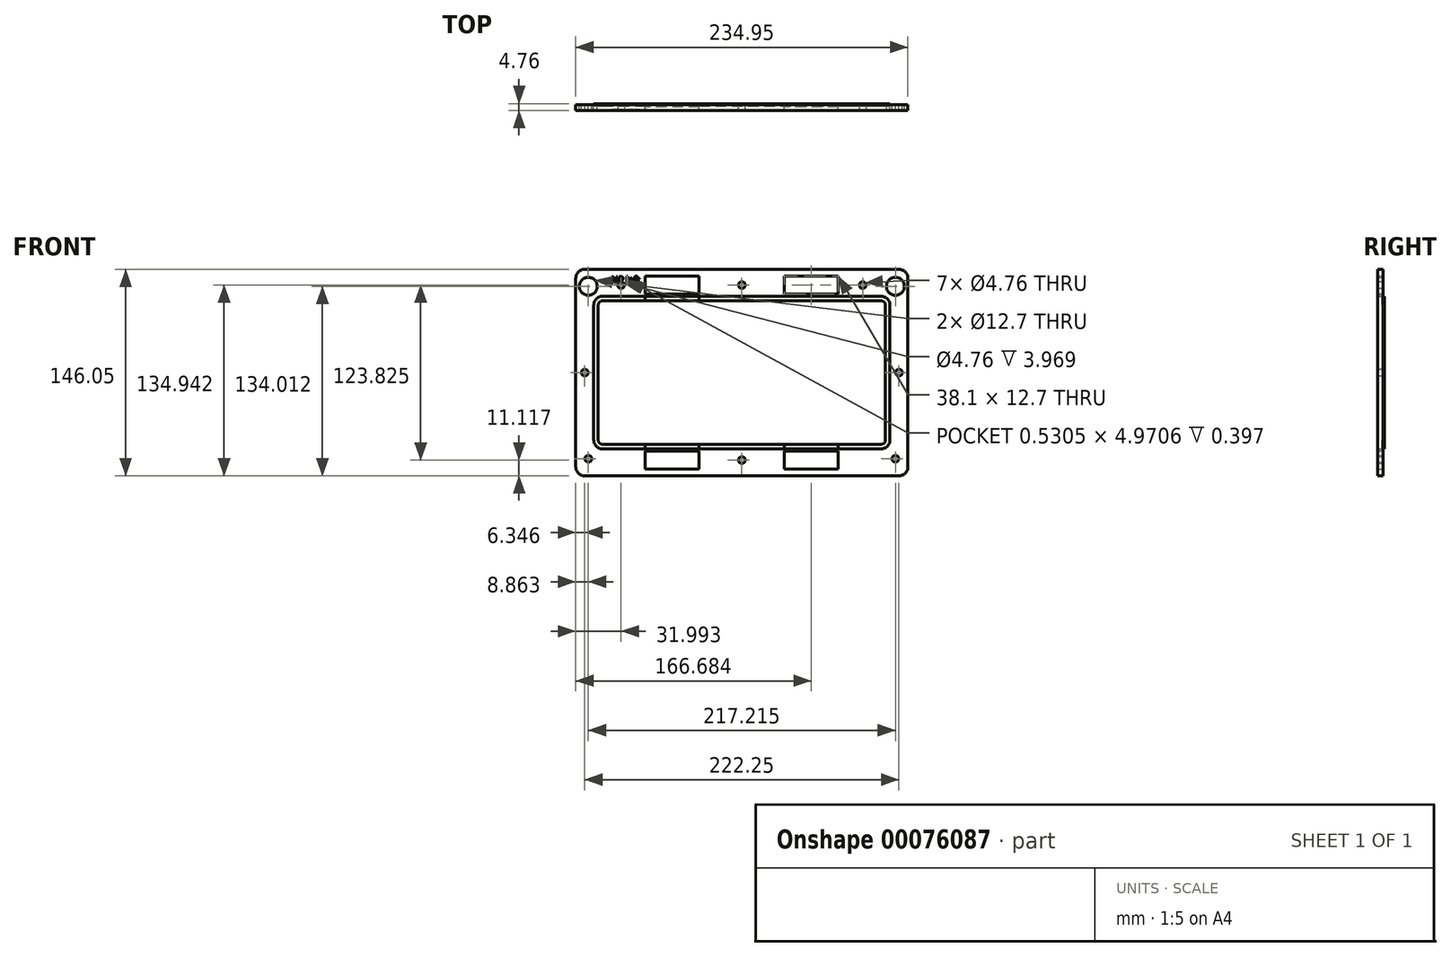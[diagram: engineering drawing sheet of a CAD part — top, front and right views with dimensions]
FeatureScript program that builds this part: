
annotation { "Feature Type Name" : "Feature", "Feature Type Description" : "" }
export const myFeature = defineFeature(function(context is Context, id is Id, definition is map)
    precondition{}
    {
        {
            var Q0;
            Q0=qCreatedBy(makeId("Front.planeOp"),FACE);
            var sketch = newSketch(context, id + "F0", { "sketchPlane" : qUnion([Q0])});
            skLineSegment(sketch, "E0.bottom", {"start": v(-85.43, 54.25) * mm, "end": v(111.42, 54.25) * mm});
            skLineSegment(sketch, "E0.top", {"start": v(-85.43, -53.7) * mm, "end": v(111.42, -53.7) * mm});
            skLineSegment(sketch, "E0.left", {"start": v(-91.78, 47.9) * mm, "end": v(-91.78, -47.35) * mm});
            skLineSegment(sketch, "E0.right", {"start": v(117.77, 47.9) * mm, "end": v(117.77, -47.35) * mm});
            skPoint(sketch, "E1.visualSharp", {"position": v(-91.78, 54.25) * mm});
            skArc(sketch, "E1.filletArc", {"start": v(-85.43, 54.25) * mm, "mid": v(-89.92, 52.4) * mm, "end": v(-91.78, 47.9) * mm});
            skPoint(sketch, "E2.visualSharp", {"position": v(117.77, 54.25) * mm});
            skArc(sketch, "E2.filletArc", {"start": v(117.77, 47.9) * mm, "mid": v(115.9, 52.4) * mm, "end": v(111.42, 54.25) * mm});
            skPoint(sketch, "E3.visualSharp", {"position": v(117.77, -53.7) * mm});
            skArc(sketch, "E3.filletArc", {"start": v(111.42, -53.7) * mm, "mid": v(115.9, -51.84) * mm, "end": v(117.77, -47.35) * mm});
            skPoint(sketch, "E4.visualSharp", {"position": v(-91.78, -53.7) * mm});
            skArc(sketch, "E4.filletArc", {"start": v(-91.78, -47.35) * mm, "mid": v(-89.92, -51.84) * mm, "end": v(-85.43, -53.7) * mm});
            skArc(sketch, "E5.0", {"start": v(-85.43, 51.08) * mm, "mid": v(-87.68, 50.15) * mm, "end": v(-88.6, 47.9) * mm});
            skLineSegment(sketch, "E5.1", {"start": v(-88.6, 47.9) * mm, "end": v(-88.6, -47.35) * mm});
            skLineSegment(sketch, "E5.2", {"start": v(-85.43, 51.08) * mm, "end": v(111.42, 51.08) * mm});
            skArc(sketch, "E5.3", {"start": v(-88.6, -47.35) * mm, "mid": v(-87.68, -49.6) * mm, "end": v(-85.43, -50.52) * mm});
            skArc(sketch, "E5.4", {"start": v(114.6, 47.9) * mm, "mid": v(113.66, 50.15) * mm, "end": v(111.42, 51.08) * mm});
            skLineSegment(sketch, "E5.5", {"start": v(114.6, 47.9) * mm, "end": v(114.6, -47.35) * mm});
            skArc(sketch, "E5.6", {"start": v(111.42, -50.52) * mm, "mid": v(113.66, -49.6) * mm, "end": v(114.6, -47.35) * mm});
            skLineSegment(sketch, "E5.7", {"start": v(-85.43, -50.52) * mm, "end": v(111.42, -50.52) * mm});
            skLineSegment(sketch, "E6.0", {"start": v(-98.13, 73.3) * mm, "end": v(124.12, 73.3) * mm});
            skLineSegment(sketch, "E7.0", {"start": v(-98.13, -72.75) * mm, "end": v(124.12, -72.75) * mm});
            skLineSegment(sketch, "E8.0", {"start": v(-104.48, 66.95) * mm, "end": v(-104.48, -66.4) * mm});
            skLineSegment(sketch, "E9.0", {"start": v(130.47, 66.95) * mm, "end": v(130.47, -66.4) * mm});
            skPoint(sketch, "E10.visualSharp", {"position": v(-104.48, 73.3) * mm});
            skArc(sketch, "E10.filletArc", {"start": v(-98.13, 73.3) * mm, "mid": v(-102.62, 71.44) * mm, "end": v(-104.48, 66.95) * mm});
            skPoint(sketch, "E11.visualSharp", {"position": v(130.47, 73.3) * mm});
            skArc(sketch, "E11.filletArc", {"start": v(130.47, 66.95) * mm, "mid": v(128.6, 71.44) * mm, "end": v(124.12, 73.3) * mm});
            skPoint(sketch, "E12.visualSharp", {"position": v(130.47, -72.75) * mm});
            skArc(sketch, "E12.filletArc", {"start": v(124.12, -72.75) * mm, "mid": v(128.6, -70.89) * mm, "end": v(130.47, -66.4) * mm});
            skPoint(sketch, "E13.visualSharp", {"position": v(-104.48, -72.75) * mm});
            skArc(sketch, "E13.filletArc", {"start": v(-104.48, -66.4) * mm, "mid": v(-102.62, -70.89) * mm, "end": v(-98.13, -72.75) * mm});
            skLineSegment(sketch, "E14", {"start": v(-104.48, 66.95) * mm, "end": v(-98.13, 73.3) * mm, "construction": true});
            skLineSegment(sketch, "E15", {"start": v(-101.3, 70.13) * mm, "end": v(-89.92, 52.4) * mm, "construction": true});
            skLineSegment(sketch, "E16", {"start": v(-104.48, 0.28) * mm, "end": v(-91.78, 0.28) * mm, "construction": true});
            skLineSegment(sketch, "E17", {"start": v(-98.13, -72.75) * mm, "end": v(-104.48, -66.4) * mm, "construction": true});
            skLineSegment(sketch, "E18", {"start": v(-101.3, -69.57) * mm, "end": v(-89.92, -51.84) * mm, "construction": true});
            skLineSegment(sketch, "E19", {"start": v(13, 94.6) * mm, "end": v(13, -140.03) * mm, "construction": true});
            skPoint(sketch, "E19.startSnap0", {"position": v(13, 73.3) * mm});
            skLineSegment(sketch, "E20", {"start": v(-149.83, 0.28) * mm, "end": v(205.44, 0.28) * mm, "construction": true});
            skLineSegment(sketch, "E21", {"start": v(-85.43, 54.25) * mm, "end": v(-85.43, 73.3) * mm, "construction": true});
            skCircle(sketch, "E22", {"center": v(-95.62, 61.26) * mm, "radius": 6.35 * mm});
            skCircle(sketch, "E23", {"center": v(-98.13, 0.28) * mm, "radius": 2.38 * mm});
            skCircle(sketch, "E24", {"center": v(-95.62, -60.7) * mm, "radius": 2.38 * mm});
            skLineSegment(sketch, "E25", {"start": v(-85.43, -53.7) * mm, "end": v(-85.43, -72.75) * mm, "construction": true});
            skLineSegment(sketch, "E26", {"start": v(-85.43, -72.75) * mm, "end": v(-85.43, -63.22) * mm, "construction": true});
            skLineSegment(sketch, "E27", {"start": v(-85.43, -63.22) * mm, "end": v(39.92, -63.22) * mm, "construction": true});
            skLineSegment(sketch, "E28", {"start": v(13, 54.25) * mm, "end": v(13, 73.3) * mm, "construction": true});
            skLineSegment(sketch, "E29", {"start": v(13, -72.75) * mm, "end": v(13, -53.7) * mm, "construction": true});
            skCircle(sketch, "E30", {"center": v(13, 62.2) * mm, "radius": 2.38 * mm});
            skLineSegment(sketch, "E31.bottom", {"start": v(-17.17, 55.84) * mm, "end": v(-55.27, 55.84) * mm});
            skLineSegment(sketch, "E31.top", {"start": v(-17.17, 68.54) * mm, "end": v(-55.27, 68.54) * mm});
            skLineSegment(sketch, "E31.left", {"start": v(-17.17, 55.84) * mm, "end": v(-17.17, 68.54) * mm});
            skLineSegment(sketch, "E31.right", {"start": v(-55.27, 55.84) * mm, "end": v(-55.27, 68.54) * mm});
            skPoint(sketch, "E31.middle", {"position": v(-36.22, 62.2) * mm});
            skLineSegment(sketch, "E32.MirrorCS", {"start": v(43.15, 55.84) * mm, "end": v(43.15, 68.54) * mm});
            skLineSegment(sketch, "E33.MirrorCS", {"start": v(43.15, 68.54) * mm, "end": v(81.25, 68.54) * mm});
            skLineSegment(sketch, "E34.MirrorCS", {"start": v(81.25, 55.84) * mm, "end": v(81.25, 68.54) * mm});
            skLineSegment(sketch, "E35.MirrorCS", {"start": v(43.15, 55.84) * mm, "end": v(81.25, 55.84) * mm});
            skCircle(sketch, "E36.MirrorC", {"center": v(121.6, 61.26) * mm, "radius": 6.35 * mm});
            skCircle(sketch, "E37.MirrorC", {"center": v(124.12, 0.28) * mm, "radius": 2.38 * mm});
            skCircle(sketch, "E38.MirrorC", {"center": v(121.6, -60.7) * mm, "radius": 2.38 * mm});
            skLineSegment(sketch, "E39.MirrorCS", {"start": v(-55.27, -55.28) * mm, "end": v(-55.27, -67.98) * mm});
            skLineSegment(sketch, "E40.MirrorCS", {"start": v(-17.17, -55.28) * mm, "end": v(-17.17, -67.98) * mm});
            skLineSegment(sketch, "E41.MirrorCS", {"start": v(-17.17, -55.28) * mm, "end": v(-55.27, -55.28) * mm});
            skLineSegment(sketch, "E42.MirrorCS", {"start": v(-17.17, -67.98) * mm, "end": v(-55.27, -67.98) * mm});
            skCircle(sketch, "E43.MirrorC", {"center": v(13, -61.63) * mm, "radius": 2.38 * mm});
            skLineSegment(sketch, "E44.MirrorCS", {"start": v(43.15, -55.28) * mm, "end": v(43.15, -67.98) * mm});
            skLineSegment(sketch, "E45.MirrorCS", {"start": v(43.15, -67.98) * mm, "end": v(81.25, -67.98) * mm});
            skLineSegment(sketch, "E46.MirrorCS", {"start": v(81.25, -55.28) * mm, "end": v(81.25, -67.98) * mm});
            skLineSegment(sketch, "E47.MirrorCS", {"start": v(43.15, -55.28) * mm, "end": v(81.25, -55.28) * mm});
            skSolve(sketch);
        }
        {
            var Q0;
            Q0 = qSketchRegion(id + "F0", true);
            var Q1;
            Q1=makeQuery(id+"F0.imprint","IMPRINT",FACE,{"disambiguationData":[TD([[makeQuery(id+"F0.imprint","IMPRINT",EDGE,{"derivedFrom":sQuery(id+"F0.wireOp",EDGE,"E0.bottom")}),-1.0]])]});
            extrude(context, id + "F1", {"entities" : qUnion([Q0, Q1]), "depth" : 0.8 * mm});
        }
        {
            var Q0;
            Q0=makeQuery(id+"F1.opExtrude","CAP_FACE",FACE,{"disambiguationData":[OSD([sQuery(id+"F0.wireOp",EDGE,"E5.0"),sQuery(id+"F0.wireOp",EDGE,"E5.1"),sQuery(id+"F0.wireOp",EDGE,"E5.2"),sQuery(id+"F0.wireOp",EDGE,"E5.3"),sQuery(id+"F0.wireOp",EDGE,"E5.4"),sQuery(id+"F0.wireOp",EDGE,"E5.5"),sQuery(id+"F0.wireOp",EDGE,"E5.6"),sQuery(id+"F0.wireOp",EDGE,"E5.7"),sQuery(id+"F0.wireOp",EDGE,"E6.0"),sQuery(id+"F0.wireOp",EDGE,"E7.0"),sQuery(id+"F0.wireOp",EDGE,"E8.0"),sQuery(id+"F0.wireOp",EDGE,"E9.0"),sQuery(id+"F0.wireOp",EDGE,"E10.filletArc"),sQuery(id+"F0.wireOp",EDGE,"E11.filletArc"),sQuery(id+"F0.wireOp",EDGE,"E12.filletArc"),sQuery(id+"F0.wireOp",EDGE,"E13.filletArc"),sQuery(id+"F0.wireOp",EDGE,"E22"),sQuery(id+"F0.wireOp",EDGE,"E23"),sQuery(id+"F0.wireOp",EDGE,"E24"),sQuery(id+"F0.wireOp",EDGE,"E30"),sQuery(id+"F0.wireOp",EDGE,"E31.bottom"),sQuery(id+"F0.wireOp",EDGE,"E31.top"),sQuery(id+"F0.wireOp",EDGE,"E31.left"),sQuery(id+"F0.wireOp",EDGE,"E31.right"),sQuery(id+"F0.wireOp",EDGE,"E32.MirrorCS"),sQuery(id+"F0.wireOp",EDGE,"E33.MirrorCS"),sQuery(id+"F0.wireOp",EDGE,"E34.MirrorCS"),sQuery(id+"F0.wireOp",EDGE,"E35.MirrorCS"),sQuery(id+"F0.wireOp",EDGE,"E36.MirrorC"),sQuery(id+"F0.wireOp",EDGE,"E37.MirrorC"),sQuery(id+"F0.wireOp",EDGE,"E38.MirrorC"),sQuery(id+"F0.wireOp",EDGE,"E39.MirrorCS"),sQuery(id+"F0.wireOp",EDGE,"E40.MirrorCS"),sQuery(id+"F0.wireOp",EDGE,"E41.MirrorCS"),sQuery(id+"F0.wireOp",EDGE,"E42.MirrorCS"),sQuery(id+"F0.wireOp",EDGE,"E43.MirrorC"),sQuery(id+"F0.wireOp",EDGE,"E44.MirrorCS"),sQuery(id+"F0.wireOp",EDGE,"E45.MirrorCS"),sQuery(id+"F0.wireOp",EDGE,"E46.MirrorCS"),sQuery(id+"F0.wireOp",EDGE,"E47.MirrorCS")])],"isStart":false});
            var sketch = newSketch(context, id + "F2", { "sketchPlane" : qUnion([Q0])});
            skLineSegment(sketch, "E48.0", {"start": v(-85.43, 54.25) * mm, "end": v(111.42, 54.25) * mm});
            skLineSegment(sketch, "E49.0", {"start": v(-85.43, -53.7) * mm, "end": v(111.42, -53.7) * mm});
            skLineSegment(sketch, "E50", {"start": v(-91.78, 47.9) * mm, "end": v(-91.78, -47.35) * mm});
            skLineSegment(sketch, "E51", {"start": v(117.77, 47.9) * mm, "end": v(117.77, -47.35) * mm});
            skPoint(sketch, "E52.visualSharp", {"position": v(-91.78, 54.25) * mm});
            skArc(sketch, "E52.filletArc", {"start": v(-85.43, 54.25) * mm, "mid": v(-89.92, 52.4) * mm, "end": v(-91.78, 47.9) * mm});
            skPoint(sketch, "E53.visualSharp", {"position": v(117.77, 54.25) * mm});
            skArc(sketch, "E53.filletArc", {"start": v(117.77, 47.9) * mm, "mid": v(115.9, 52.4) * mm, "end": v(111.42, 54.25) * mm});
            skPoint(sketch, "E54.visualSharp", {"position": v(117.77, -53.7) * mm});
            skArc(sketch, "E54.filletArc", {"start": v(111.42, -53.7) * mm, "mid": v(115.9, -51.84) * mm, "end": v(117.77, -47.35) * mm});
            skPoint(sketch, "E55.visualSharp", {"position": v(-91.78, -53.7) * mm});
            skArc(sketch, "E55.filletArc", {"start": v(-91.78, -47.35) * mm, "mid": v(-89.92, -51.84) * mm, "end": v(-85.43, -53.7) * mm});
            skSolve(sketch);
        }
        {
            var Q0;
            Q0=makeQuery(id+"F2.imprint","IMPRINT",FACE,{"disambiguationData":[TD([[makeQuery(id+"F2.imprint","IMPRINT",EDGE,{"derivedFrom":sQuery(id+"F2.wireOp",EDGE,"E48.0")}),1.0]])]});
            extrude(context, id + "F3", {"entities" : qUnion([Q0]), "operationType" : NewBodyOperationType.ADD, "depth" : 3.17 * mm});
        }
        {
            var Q0;
            Q0=makeQuery(id+"F1.opExtrude","CAP_FACE",FACE,{"disambiguationData":[OSD([sQuery(id+"F0.wireOp",EDGE,"E5.0"),sQuery(id+"F0.wireOp",EDGE,"E5.1"),sQuery(id+"F0.wireOp",EDGE,"E5.2"),sQuery(id+"F0.wireOp",EDGE,"E5.3"),sQuery(id+"F0.wireOp",EDGE,"E5.4"),sQuery(id+"F0.wireOp",EDGE,"E5.5"),sQuery(id+"F0.wireOp",EDGE,"E5.6"),sQuery(id+"F0.wireOp",EDGE,"E5.7"),sQuery(id+"F0.wireOp",EDGE,"E6.0"),sQuery(id+"F0.wireOp",EDGE,"E7.0"),sQuery(id+"F0.wireOp",EDGE,"E8.0"),sQuery(id+"F0.wireOp",EDGE,"E9.0"),sQuery(id+"F0.wireOp",EDGE,"E10.filletArc"),sQuery(id+"F0.wireOp",EDGE,"E11.filletArc"),sQuery(id+"F0.wireOp",EDGE,"E12.filletArc"),sQuery(id+"F0.wireOp",EDGE,"E13.filletArc"),sQuery(id+"F0.wireOp",EDGE,"E22"),sQuery(id+"F0.wireOp",EDGE,"E23"),sQuery(id+"F0.wireOp",EDGE,"E24"),sQuery(id+"F0.wireOp",EDGE,"E30"),sQuery(id+"F0.wireOp",EDGE,"E31.bottom"),sQuery(id+"F0.wireOp",EDGE,"E31.top"),sQuery(id+"F0.wireOp",EDGE,"E31.left"),sQuery(id+"F0.wireOp",EDGE,"E31.right"),sQuery(id+"F0.wireOp",EDGE,"E32.MirrorCS"),sQuery(id+"F0.wireOp",EDGE,"E33.MirrorCS"),sQuery(id+"F0.wireOp",EDGE,"E34.MirrorCS"),sQuery(id+"F0.wireOp",EDGE,"E35.MirrorCS"),sQuery(id+"F0.wireOp",EDGE,"E36.MirrorC"),sQuery(id+"F0.wireOp",EDGE,"E37.MirrorC"),sQuery(id+"F0.wireOp",EDGE,"E38.MirrorC"),sQuery(id+"F0.wireOp",EDGE,"E39.MirrorCS"),sQuery(id+"F0.wireOp",EDGE,"E40.MirrorCS"),sQuery(id+"F0.wireOp",EDGE,"E41.MirrorCS"),sQuery(id+"F0.wireOp",EDGE,"E42.MirrorCS"),sQuery(id+"F0.wireOp",EDGE,"E43.MirrorC"),sQuery(id+"F0.wireOp",EDGE,"E44.MirrorCS"),sQuery(id+"F0.wireOp",EDGE,"E45.MirrorCS"),sQuery(id+"F0.wireOp",EDGE,"E46.MirrorCS"),sQuery(id+"F0.wireOp",EDGE,"E47.MirrorCS")])],"isStart":true});
            var sketch = newSketch(context, id + "F4", { "sketchPlane" : qUnion([Q0])});
            skArc(sketch, "E56.0", {"start": v(-111.42, 54.25) * mm, "mid": v(-115.9, 52.4) * mm, "end": v(-117.77, 47.9) * mm});
            skLineSegment(sketch, "E56.1", {"start": v(-117.77, 47.9) * mm, "end": v(-117.77, -47.35) * mm});
            skLineSegment(sketch, "E56.2", {"start": v(-111.42, 54.25) * mm, "end": v(85.43, 54.25) * mm});
            skArc(sketch, "E56.3", {"start": v(-117.77, -47.35) * mm, "mid": v(-115.9, -51.84) * mm, "end": v(-111.42, -53.7) * mm});
            skArc(sketch, "E56.4", {"start": v(91.78, 47.9) * mm, "mid": v(89.92, 52.4) * mm, "end": v(85.43, 54.25) * mm});
            skLineSegment(sketch, "E56.5", {"start": v(91.78, 47.9) * mm, "end": v(91.78, -47.35) * mm});
            skArc(sketch, "E56.6", {"start": v(85.43, -53.7) * mm, "mid": v(89.92, -51.84) * mm, "end": v(91.78, -47.35) * mm});
            skLineSegment(sketch, "E56.7", {"start": v(-111.42, -53.7) * mm, "end": v(85.43, -53.7) * mm});
            skArc(sketch, "E57.0", {"start": v(88.6, 47.9) * mm, "mid": v(87.68, 50.15) * mm, "end": v(85.43, 51.08) * mm});
            skLineSegment(sketch, "E57.1", {"start": v(-111.42, 51.08) * mm, "end": v(85.43, 51.08) * mm});
            skLineSegment(sketch, "E57.2", {"start": v(88.6, 47.9) * mm, "end": v(88.6, -47.35) * mm});
            skArc(sketch, "E57.3", {"start": v(-111.42, 51.08) * mm, "mid": v(-113.66, 50.15) * mm, "end": v(-114.6, 47.9) * mm});
            skArc(sketch, "E57.4", {"start": v(85.43, -50.52) * mm, "mid": v(87.68, -49.6) * mm, "end": v(88.6, -47.35) * mm});
            skLineSegment(sketch, "E57.5", {"start": v(-111.42, -50.52) * mm, "end": v(85.43, -50.52) * mm});
            skArc(sketch, "E57.6", {"start": v(-114.6, -47.35) * mm, "mid": v(-113.66, -49.6) * mm, "end": v(-111.42, -50.52) * mm});
            skLineSegment(sketch, "E57.7", {"start": v(-114.6, 47.9) * mm, "end": v(-114.6, -47.35) * mm});
            skSolve(sketch);
        }
        {
            var Q0;
            Q0 = qSketchRegion(id + "F4", true);
            extrude(context, id + "F5", {"entities" : qUnion([Q0]), "operationType" : NewBodyOperationType.ADD, "depth" : 0.8 * mm});
        }
        {
            var Q0;
            Q0=makeQuery(id+"F1.opExtrude","CAP_FACE",FACE,{"disambiguationData":[OSD([sQuery(id+"F0.wireOp",EDGE,"E5.0"),sQuery(id+"F0.wireOp",EDGE,"E5.1"),sQuery(id+"F0.wireOp",EDGE,"E5.2"),sQuery(id+"F0.wireOp",EDGE,"E5.3"),sQuery(id+"F0.wireOp",EDGE,"E5.4"),sQuery(id+"F0.wireOp",EDGE,"E5.5"),sQuery(id+"F0.wireOp",EDGE,"E5.6"),sQuery(id+"F0.wireOp",EDGE,"E5.7"),sQuery(id+"F0.wireOp",EDGE,"E6.0"),sQuery(id+"F0.wireOp",EDGE,"E7.0"),sQuery(id+"F0.wireOp",EDGE,"E8.0"),sQuery(id+"F0.wireOp",EDGE,"E9.0"),sQuery(id+"F0.wireOp",EDGE,"E10.filletArc"),sQuery(id+"F0.wireOp",EDGE,"E11.filletArc"),sQuery(id+"F0.wireOp",EDGE,"E12.filletArc"),sQuery(id+"F0.wireOp",EDGE,"E13.filletArc"),sQuery(id+"F0.wireOp",EDGE,"E22"),sQuery(id+"F0.wireOp",EDGE,"E23"),sQuery(id+"F0.wireOp",EDGE,"E24"),sQuery(id+"F0.wireOp",EDGE,"E30"),sQuery(id+"F0.wireOp",EDGE,"E31.bottom"),sQuery(id+"F0.wireOp",EDGE,"E31.top"),sQuery(id+"F0.wireOp",EDGE,"E31.left"),sQuery(id+"F0.wireOp",EDGE,"E31.right"),sQuery(id+"F0.wireOp",EDGE,"E32.MirrorCS"),sQuery(id+"F0.wireOp",EDGE,"E33.MirrorCS"),sQuery(id+"F0.wireOp",EDGE,"E34.MirrorCS"),sQuery(id+"F0.wireOp",EDGE,"E35.MirrorCS"),sQuery(id+"F0.wireOp",EDGE,"E36.MirrorC"),sQuery(id+"F0.wireOp",EDGE,"E37.MirrorC"),sQuery(id+"F0.wireOp",EDGE,"E38.MirrorC"),sQuery(id+"F0.wireOp",EDGE,"E39.MirrorCS"),sQuery(id+"F0.wireOp",EDGE,"E40.MirrorCS"),sQuery(id+"F0.wireOp",EDGE,"E41.MirrorCS"),sQuery(id+"F0.wireOp",EDGE,"E42.MirrorCS"),sQuery(id+"F0.wireOp",EDGE,"E43.MirrorC"),sQuery(id+"F0.wireOp",EDGE,"E44.MirrorCS"),sQuery(id+"F0.wireOp",EDGE,"E45.MirrorCS"),sQuery(id+"F0.wireOp",EDGE,"E46.MirrorCS"),sQuery(id+"F0.wireOp",EDGE,"E47.MirrorCS")])],"isStart":true});
            var sketch = newSketch(context, id + "F6", { "sketchPlane" : qUnion([Q0])});
            skLineSegment(sketch, "E58.bottom", {"start": v(-81.26, -55.28) * mm, "end": v(-43.16, -55.28) * mm});
            skLineSegment(sketch, "E58.top", {"start": v(-81.26, -50.18) * mm, "end": v(-43.16, -50.18) * mm});
            skLineSegment(sketch, "E58.left", {"start": v(-81.26, -55.28) * mm, "end": v(-81.26, -50.18) * mm});
            skLineSegment(sketch, "E58.right", {"start": v(-43.16, -55.28) * mm, "end": v(-43.16, -50.18) * mm});
            skLineSegment(sketch, "E59", {"start": v(-13, -90.5) * mm, "end": v(-13, 104.82) * mm, "construction": true});
            skPoint(sketch, "E59.startSnap0", {"position": v(-13, -53.7) * mm});
            skLineSegment(sketch, "E60.MirrorCS", {"start": v(55.27, -55.28) * mm, "end": v(55.27, -50.18) * mm});
            skLineSegment(sketch, "E61.MirrorCS", {"start": v(17.18, -55.28) * mm, "end": v(17.18, -50.18) * mm});
            skLineSegment(sketch, "E62.MirrorCS", {"start": v(55.27, -55.28) * mm, "end": v(17.18, -55.28) * mm});
            skLineSegment(sketch, "E63.MirrorCS", {"start": v(55.27, -50.18) * mm, "end": v(17.18, -50.18) * mm});
            skLineSegment(sketch, "E64.bottom", {"start": v(17.17, 55.84) * mm, "end": v(55.29, 55.84) * mm});
            skLineSegment(sketch, "E64.top", {"start": v(17.17, 50.06) * mm, "end": v(55.29, 50.06) * mm});
            skLineSegment(sketch, "E64.left", {"start": v(17.17, 55.84) * mm, "end": v(17.17, 50.06) * mm});
            skLineSegment(sketch, "E64.right", {"start": v(55.29, 55.84) * mm, "end": v(55.29, 50.06) * mm});
            skSolve(sketch);
        }
        {
            var Q0;
            Q0 = qSketchRegion(id + "F6", true);
            extrude(context, id + "F7", {"entities" : qUnion([Q0]), "operationType" : NewBodyOperationType.REMOVE, "oppositeDirection" : true, "depth" : 1.59 * mm});
        }
        {
            var Q0;
            Q0=makeQuery(id+"F3.opExtrude","CAP_FACE",FACE,{"disambiguationData":[OSD([sQuery(id+"F0.wireOp",EDGE,"E6.0"),sQuery(id+"F0.wireOp",EDGE,"E7.0"),sQuery(id+"F0.wireOp",EDGE,"E8.0"),sQuery(id+"F0.wireOp",EDGE,"E9.0"),sQuery(id+"F0.wireOp",EDGE,"E10.filletArc"),sQuery(id+"F0.wireOp",EDGE,"E11.filletArc"),sQuery(id+"F0.wireOp",EDGE,"E12.filletArc"),sQuery(id+"F0.wireOp",EDGE,"E13.filletArc"),sQuery(id+"F0.wireOp",EDGE,"E22"),sQuery(id+"F0.wireOp",EDGE,"E23"),sQuery(id+"F0.wireOp",EDGE,"E24"),sQuery(id+"F0.wireOp",EDGE,"E30"),sQuery(id+"F0.wireOp",EDGE,"E31.bottom"),sQuery(id+"F0.wireOp",EDGE,"E31.top"),sQuery(id+"F0.wireOp",EDGE,"E31.left"),sQuery(id+"F0.wireOp",EDGE,"E31.right"),sQuery(id+"F0.wireOp",EDGE,"E32.MirrorCS"),sQuery(id+"F0.wireOp",EDGE,"E33.MirrorCS"),sQuery(id+"F0.wireOp",EDGE,"E34.MirrorCS"),sQuery(id+"F0.wireOp",EDGE,"E35.MirrorCS"),sQuery(id+"F0.wireOp",EDGE,"E36.MirrorC"),sQuery(id+"F0.wireOp",EDGE,"E37.MirrorC"),sQuery(id+"F0.wireOp",EDGE,"E38.MirrorC"),sQuery(id+"F0.wireOp",EDGE,"E39.MirrorCS"),sQuery(id+"F0.wireOp",EDGE,"E40.MirrorCS"),sQuery(id+"F0.wireOp",EDGE,"E41.MirrorCS"),sQuery(id+"F0.wireOp",EDGE,"E42.MirrorCS"),sQuery(id+"F0.wireOp",EDGE,"E43.MirrorC"),sQuery(id+"F0.wireOp",EDGE,"E44.MirrorCS"),sQuery(id+"F0.wireOp",EDGE,"E45.MirrorCS"),sQuery(id+"F0.wireOp",EDGE,"E46.MirrorCS"),sQuery(id+"F0.wireOp",EDGE,"E47.MirrorCS"),sQuery(id+"F2.wireOp",EDGE,"E48.0"),sQuery(id+"F2.wireOp",EDGE,"E49.0"),sQuery(id+"F2.wireOp",EDGE,"E50"),sQuery(id+"F2.wireOp",EDGE,"E51"),sQuery(id+"F2.wireOp",EDGE,"E52.filletArc"),sQuery(id+"F2.wireOp",EDGE,"E53.filletArc"),sQuery(id+"F2.wireOp",EDGE,"E54.filletArc"),sQuery(id+"F2.wireOp",EDGE,"E55.filletArc")])],"isStart":false});
            var sketch = newSketch(context, id + "F8", { "sketchPlane" : qUnion([Q0])});
            skText(sketch, "E65", { "text": "NP left\n", "fontName": "OpenSans-Regular.ttf"});
            const initialGuessF8  = {"E65": [-0.07952, 0.06355, 1, 0, 0.00471]};
            skSetInitialGuess(sketch, initialGuessF8);
            skSolve(sketch);
        }
        {
            var Q0;
            Q0 = qSketchRegion(id + "F8", true);
            extrude(context, id + "F9", {"entities" : qUnion([Q0]), "operationType" : NewBodyOperationType.REMOVE, "oppositeDirection" : true, "depth" : 0.4 * mm});
        }
        {
            var Q0;
            {var subQ0=sQuery(id+"F0.wireOp",EDGE,"E12.filletArc");var subQ1=sQuery(id+"F0.wireOp",EDGE,"E6.0");var subQ2=sQuery(id+"F0.wireOp",EDGE,"E7.0");var subQ3=sQuery(id+"F0.wireOp",EDGE,"E22");var subQ4=sQuery(id+"F0.wireOp",EDGE,"E31.top");var subQ5=sQuery(id+"F0.wireOp",EDGE,"E31.bottom");var subQ6=sQuery(id+"F0.wireOp",EDGE,"E36.MirrorC");var subQ7=sQuery(id+"F0.wireOp",EDGE,"E35.MirrorCS");var subQ8=sQuery(id+"F0.wireOp",EDGE,"E32.MirrorCS");var subQ9=sQuery(id+"F0.wireOp",EDGE,"E31.right");var subQ10=sQuery(id+"F0.wireOp",EDGE,"E46.MirrorCS");var subQ11=sQuery(id+"F0.wireOp",EDGE,"E34.MirrorCS");var subQ12=sQuery(id+"F2.wireOp",EDGE,"E54.filletArc");var subQ13=sQuery(id+"F0.wireOp",EDGE,"E23");var subQ14=sQuery(id+"F0.wireOp",EDGE,"E30");var subQ15=sQuery(id+"F0.wireOp",EDGE,"E31.left");var subQ16=sQuery(id+"F0.wireOp",EDGE,"E13.filletArc");var subQ17=sQuery(id+"F0.wireOp",EDGE,"E37.MirrorC");var subQ18=sQuery(id+"F0.wireOp",EDGE,"E43.MirrorC");var subQ19=sQuery(id+"F0.wireOp",EDGE,"E40.MirrorCS");var subQ20=sQuery(id+"F0.wireOp",EDGE,"E45.MirrorCS");var subQ21=sQuery(id+"F0.wireOp",EDGE,"E39.MirrorCS");var subQ22=sQuery(id+"F0.wireOp",EDGE,"E8.0");var subQ23=sQuery(id+"F0.wireOp",EDGE,"E47.MirrorCS");var subQ24=sQuery(id+"F0.wireOp",EDGE,"E24");var subQ25=sQuery(id+"F0.wireOp",EDGE,"E9.0");var subQ26=sQuery(id+"F0.wireOp",EDGE,"E10.filletArc");var subQ27=sQuery(id+"F0.wireOp",EDGE,"E42.MirrorCS");var subQ28=sQuery(id+"F0.wireOp",EDGE,"E33.MirrorCS");var subQ29=sQuery(id+"F0.wireOp",EDGE,"E11.filletArc");var subQ30=sQuery(id+"F0.wireOp",EDGE,"E38.MirrorC");var subQ31=sQuery(id+"F0.wireOp",EDGE,"E41.MirrorCS");var subQ32=sQuery(id+"F0.wireOp",EDGE,"E44.MirrorCS");var subQ33=sQuery(id+"F2.wireOp",EDGE,"E48.0");var subQ34=sQuery(id+"F2.wireOp",EDGE,"E49.0");var subQ35=sQuery(id+"F2.wireOp",EDGE,"E50");var subQ36=sQuery(id+"F2.wireOp",EDGE,"E51");var subQ37=sQuery(id+"F2.wireOp",EDGE,"E55.filletArc");var subQ38=sQuery(id+"F2.wireOp",EDGE,"E52.filletArc");var subQ39=sQuery(id+"F2.wireOp",EDGE,"E53.filletArc");Q0=makeQuery(id+"F9.boolean.opBoolean","SPLIT",FACE,{"disambiguationData":[TD([makeQuery(id+"F1.opExtrude","SWEPT_FACE",FACE,{"disambiguationData":[OSD([subQ1])]})])],"derivedFrom":makeQuery(id+"F3.opExtrude","CAP_FACE",FACE,{"disambiguationData":[OSD([subQ1,subQ2,subQ22,subQ25,subQ26,subQ29,subQ0,subQ16,subQ3,subQ13,subQ24,subQ14,subQ5,subQ4,subQ15,subQ9,subQ8,subQ28,subQ11,subQ7,subQ6,subQ17,subQ30,subQ21,subQ19,subQ31,subQ27,subQ18,subQ32,subQ20,subQ10,subQ23,subQ33,subQ34,subQ35,subQ36,subQ38,subQ39,subQ12,subQ37])],"isStart":false})});}
            var sketch = newSketch(context, id + "F10", { "sketchPlane" : qUnion([Q0])});
            skCircle(sketch, "E66", {"center": v(-72.49, 62.2) * mm, "radius": 2.38 * mm});
            skLineSegment(sketch, "E67", {"start": v(13, 73.3) * mm, "end": v(13, -72.75) * mm, "construction": true});
            skLineSegment(sketch, "E68", {"start": v(13, -72.75) * mm, "end": v(14.17, -73.1) * mm, "construction": true});
            skLineSegment(sketch, "E69", {"start": v(-104.48, 0.28) * mm, "end": v(130.47, 0.28) * mm, "construction": true});
            skCircle(sketch, "E70.MirrorC", {"center": v(98.47, 62.2) * mm, "radius": 2.38 * mm});
            skSolve(sketch);
        }
        {
            var Q0;
            Q0 = qSketchRegion(id + "F10", true);
            extrude(context, id + "F11", {"entities" : qUnion([Q0]), "operationType" : NewBodyOperationType.REMOVE, "oppositeDirection" : true, "depth" : 25.4 * mm});
        }
    });
